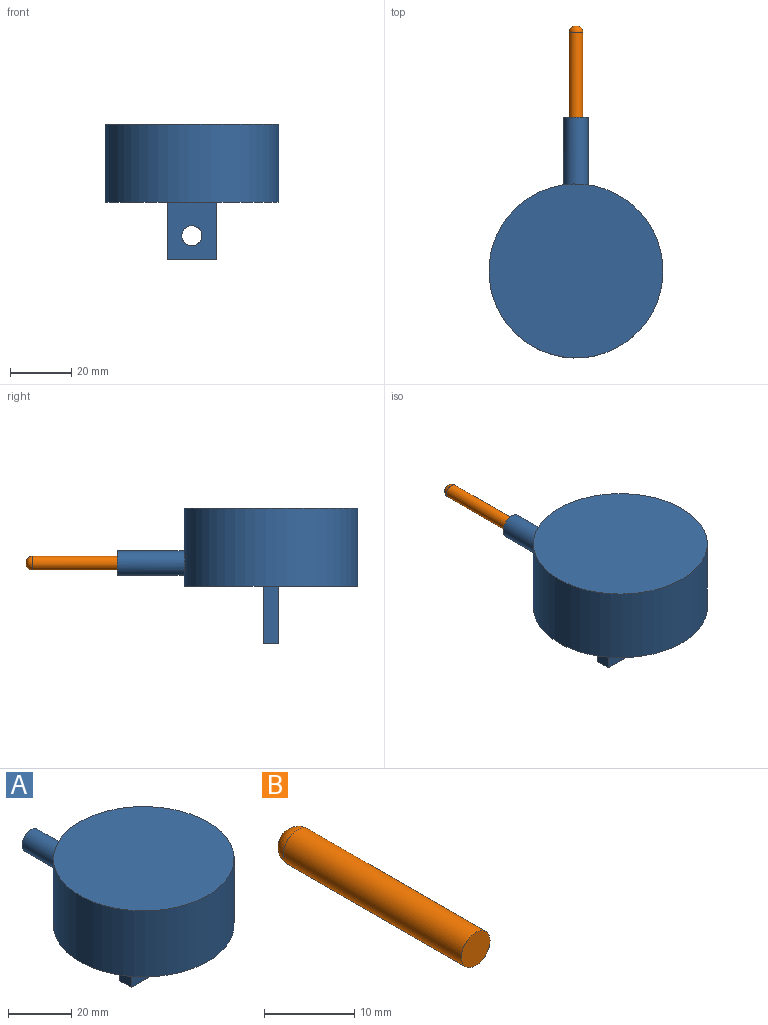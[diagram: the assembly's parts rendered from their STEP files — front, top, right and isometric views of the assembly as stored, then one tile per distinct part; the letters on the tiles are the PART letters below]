
ASSEMBLY  parts=2 mates=1
PART A: 13 faces, bbox 57x78.8x44.4 mm
  f0: cylinder r=28.5mm len=57mm, axis (0,0,-1), area 4519.6mm2, adj f1,f2,f9
  f1: plane 57x57mm, normal (0,0,-1), area 2470.5mm2, adj f0,f3,f4,f5,f6
  f2: plane 57x57mm, normal (0,0,1), area 2551.8mm2, adj f0
  f3: plane 18.85x5mm, normal (-1,0,0), area 94.2mm2, adj f1,f4,f6,f7
  f4: plane 18.85x16.25mm, normal (0,1,0), area 272.1mm2, adj f1,f3,f5,f7,f8
  f5: plane 18.85x5mm, normal (1,0,0), area 94.2mm2, adj f1,f4,f6,f7
  f6: plane 18.85x16.25mm, normal (0,-1,0), area 272.1mm2, adj f1,f3,f5,f7,f8
  f7: plane 16.25x5mm, normal (0,0,-1), area 81.3mm2, adj f3,f4,f5,f6
  f8: cylinder r=3.3mm len=6.6mm, axis (0,1,0), area 103.7mm2, adj f4,f6
  f9: cylinder r=3.98mm len=22.12mm, axis (0,1,0), area 549.6mm2, adj f0,f10
  f10: plane 7.96x7.96mm, normal (0,1,0), area 33.9mm2, adj f9,f12
  f11: plane 4.5x4.5mm, normal (0,1,0), area 15.9mm2, adj f12
  f12: cylinder r=2.25mm len=21.84mm, axis (0,1,0), area 308.8mm2, adj f10,f11
PART B: 4 faces, bbox 4.5x29.9x4.5 mm
  f0: cylinder r=2.25mm len=27.94mm, axis (0,-1,0), area 395mm2, adj f2,f3
  f1: plane 0.5x0.5mm, normal (0,1,0), area 0.2mm2, adj f3
  f2: plane 4.5x4.5mm, normal (0,-1,0), area 15.9mm2, adj f0
  f3: torus R=0.25mm, axis (0,-1,0), area 30.1mm2, adj f0,f1
PLACE A t=(-12.97,-15.2,1.47)mm
PLACE B t=(38.36,35.14,-11.24)mm
MATE slider B.f0 <-> A.f9  axis (0,-1,0) through (-12.97,35.14,9.03)mm
